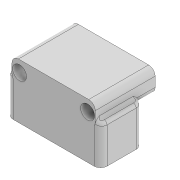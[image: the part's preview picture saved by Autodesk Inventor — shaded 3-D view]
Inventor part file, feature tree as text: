
AUTODESK INVENTOR PART (.ipt)
format: ipt  version: 2021 (Build 250183000, 183)  size: 266,240 bytes
history: native  units: mm
features: reference x6, other x5, sketch x5, extrude x3, fillet x1, hole x1, projected_geometry x1
ambient origin geometry x8: Origin, YZ Plane, XZ Plane, XY Plane, X Axis, Y Axis, Z Axis, Center Point
bodies: Body1 (feature_tree)
feature tree (22):
  other  "Твердое тело1"
  other  "РабПлоскость1"
  extrude  "Выдавливание1"  Depth=18.5mm TaperAngle=0.0deg
  extrude  "Выдавливание2"  Depth=25.0mm
  sketch  "Эскиз3"
  extrude  "Выдавливание3"  Depth=9.0mm
  fillet  "Сопряжение1"  Radius=16.0mm
  hole  "Отверстие1"  [1 undecoded]
  sketch  "Эскиз1"
  reference  "Ссылка1"
  reference  "Ссылка2"
  reference  "Ссылка3"
  reference  "Ссылка4"
  sketch  "Эскиз2"
  sketch  "Эскиз4"
  projected_geometry  "Спроецированная петля1"
  sketch  "Эскиз5"
  reference  "Ссылка5"
  reference  "Ссылка6"
  other  "<userpath>\Desktop\теплица\датчики почва воздух\Компоновка.iam"
  other  "Компоновка.iam"
  other  "Кронштейн МК:1"
note: 1 required parameter value undecoded (feature->parameter linkage not recoverable at this tier; creation-order binding heuristic only, values carry confidence <= 0.55)
